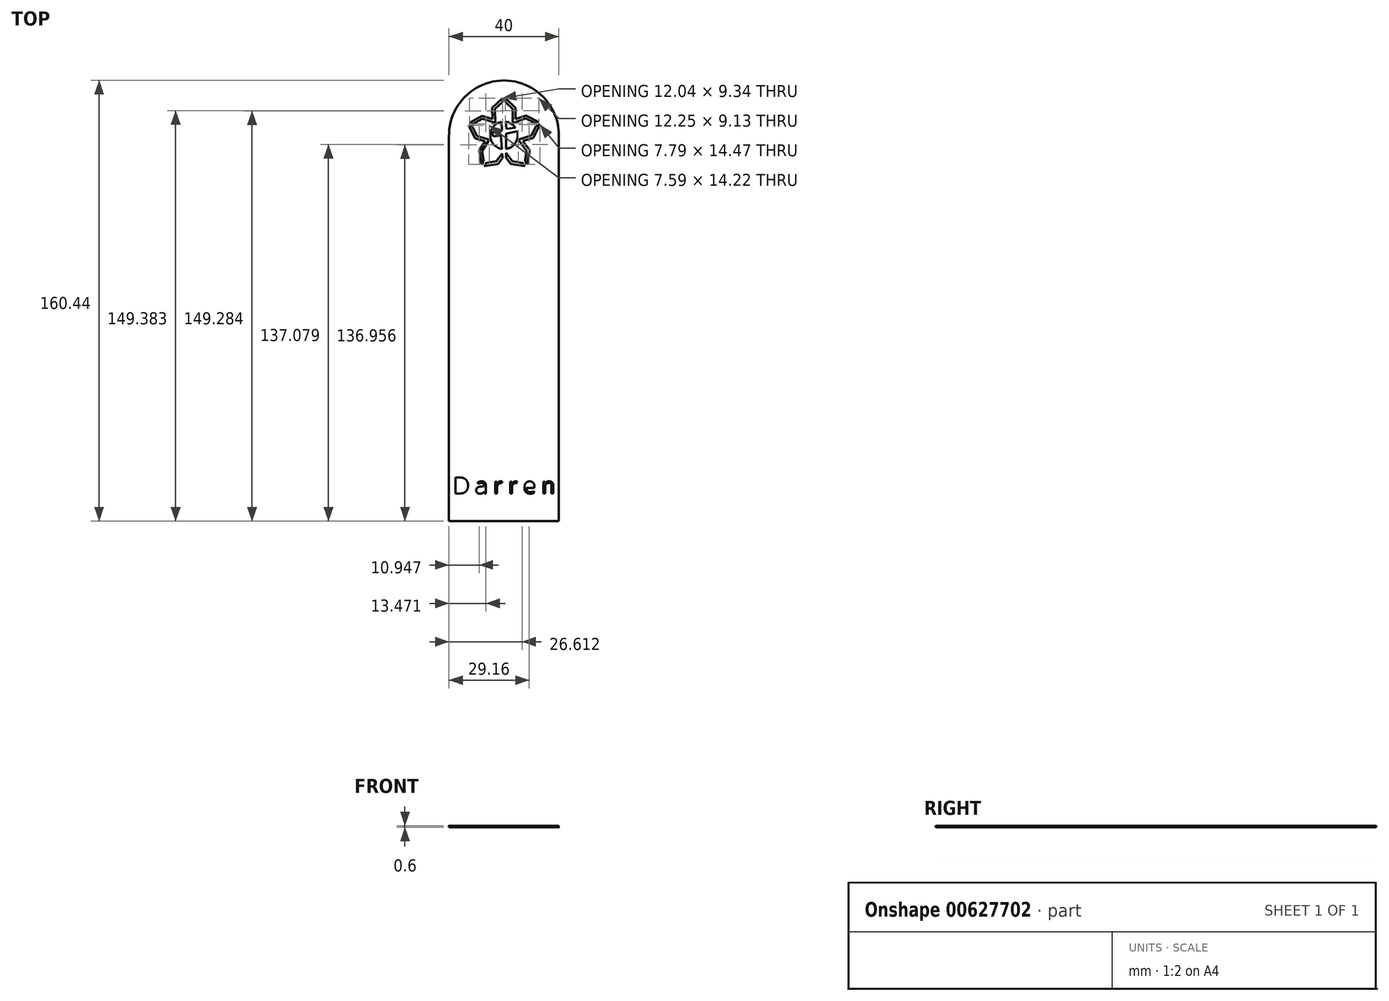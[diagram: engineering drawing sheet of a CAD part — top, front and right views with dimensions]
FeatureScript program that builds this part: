
annotation { "Feature Type Name" : "Feature", "Feature Type Description" : "" }
export const myFeature = defineFeature(function(context is Context, id is Id, definition is map)
    precondition{}
    {
        {
            var Q0;
            Q0=qCreatedBy(makeId("Top.planeOp"),FACE);
            var sketch = newSketch(context, id + "F0", { "sketchPlane" : qUnion([Q0])});
            skLineSegment(sketch, "E0", {"start": v(-29.48, 59.06) * mm, "end": v(-34.17, 60.58) * mm});
            skLineSegment(sketch, "E1", {"start": v(-34.17, 60.58) * mm, "end": v(-37.52, 58.7) * mm});
            skLineSegment(sketch, "E2", {"start": v(-37.82, 57.75) * mm, "end": v(-36.1, 54.29) * mm});
            skLineSegment(sketch, "E3", {"start": v(-36.1, 54.29) * mm, "end": v(-31.55, 52.93) * mm});
            skLineSegment(sketch, "E4", {"start": v(-31.55, 52.93) * mm, "end": v(-34.28, 48.84) * mm});
            skLineSegment(sketch, "E5", {"start": v(-34.28, 48.84) * mm, "end": v(-33.58, 45.07) * mm});
            skLineSegment(sketch, "E6", {"start": v(-32.76, 44.49) * mm, "end": v(-29.04, 45.05) * mm});
            skLineSegment(sketch, "E7", {"start": v(-29.04, 45.05) * mm, "end": v(-26.95, 47.96) * mm});
            skLineSegment(sketch, "E8", {"start": v(-25.5, 48.12) * mm, "end": v(-23.23, 45.05) * mm});
            skLineSegment(sketch, "E9", {"start": v(-23.23, 45.05) * mm, "end": v(-19.49, 44.49) * mm});
            skLineSegment(sketch, "E10", {"start": v(-18.67, 45.07) * mm, "end": v(-17.96, 48.84) * mm});
            skLineSegment(sketch, "E11", {"start": v(-17.96, 48.84) * mm, "end": v(-21.03, 52.93) * mm});
            skLineSegment(sketch, "E12", {"start": v(-21.03, 52.93) * mm, "end": v(-16.27, 54.48) * mm});
            skLineSegment(sketch, "E13", {"start": v(-16.27, 54.48) * mm, "end": v(-14.56, 57.96) * mm});
            skLineSegment(sketch, "E14", {"start": v(-14.88, 58.9) * mm, "end": v(-18.36, 60.69) * mm});
            skLineSegment(sketch, "E15", {"start": v(-18.36, 60.69) * mm, "end": v(-23.1, 59.01) * mm});
            skLineSegment(sketch, "E16", {"start": v(-23.1, 59.01) * mm, "end": v(-23.1, 64.1) * mm});
            skLineSegment(sketch, "E17", {"start": v(-23.1, 64.1) * mm, "end": v(-25.8, 66.67) * mm});
            skLineSegment(sketch, "E18", {"start": v(-26.8, 66.67) * mm, "end": v(-29.59, 64.1) * mm});
            skLineSegment(sketch, "E19", {"start": v(-29.59, 64.1) * mm, "end": v(-29.48, 59.06) * mm});
            skLineSegment(sketch, "E20", {"start": v(-25.39, 56.97) * mm, "end": v(-22.09, 57.24) * mm});
            skLineSegment(sketch, "E21", {"start": v(-25.5, 55.17) * mm, "end": v(-25.5, 49.6) * mm});
            skLineSegment(sketch, "E22", {"start": v(-26.85, 46.39) * mm, "end": v(-26.95, 47.96) * mm});
            skLineSegment(sketch, "E23", {"start": v(-27.36, 54.62) * mm, "end": v(-30.05, 54.08) * mm});
            skLineSegment(sketch, "E24", {"start": v(-30.05, 54.08) * mm, "end": v(-30.74, 55.5) * mm});
            skLineSegment(sketch, "E25", {"start": v(-30.74, 55.5) * mm, "end": v(-27.06, 56.25) * mm});
            skLineSegment(sketch, "E26", {"start": v(-27.06, 56.25) * mm, "end": v(-27.13, 59.46) * mm});
            skArc(sketch, "E27", {"start": v(-6.3, 54.09) * mm, "mid": v(-26.29, 74.53) * mm, "end": v(-46.28, 54.09) * mm});
            skLineSegment(sketch, "E28", {"start": v(-46.28, 54.09) * mm, "end": v(-46.28, -85.91) * mm});
            skLineSegment(sketch, "E29", {"start": v(-6.3, 54.09) * mm, "end": v(-6.3, -85.91) * mm});
            skLineSegment(sketch, "E30", {"start": v(-46.28, -85.91) * mm, "end": v(-6.3, -85.91) * mm});
            skLineSegment(sketch, "E31", {"start": v(-35.33, 49.06) * mm, "end": v(-33.13, 52.36) * mm});
            skLineSegment(sketch, "E32", {"start": v(-35.33, 49.06) * mm, "end": v(-34.39, 43.93) * mm});
            skLineSegment(sketch, "E33", {"start": v(-33.57, 43.35) * mm, "end": v(-28.47, 44.13) * mm});
            skLineSegment(sketch, "E34", {"start": v(-28.47, 44.13) * mm, "end": v(-26.85, 46.39) * mm});
            skLineSegment(sketch, "E35", {"start": v(-25.5, 46.44) * mm, "end": v(-23.79, 44.13) * mm});
            skLineSegment(sketch, "E36", {"start": v(-23.79, 44.13) * mm, "end": v(-18.68, 43.36) * mm});
            skLineSegment(sketch, "E37", {"start": v(-16.9, 49.09) * mm, "end": v(-17.87, 43.93) * mm});
            skLineSegment(sketch, "E38", {"start": v(-19.39, 52.41) * mm, "end": v(-16.9, 49.09) * mm});
            skLineSegment(sketch, "E39", {"start": v(-19.39, 52.41) * mm, "end": v(-15.56, 53.66) * mm});
            skLineSegment(sketch, "E40", {"start": v(-13.23, 58.4) * mm, "end": v(-15.56, 53.66) * mm});
            skLineSegment(sketch, "E41", {"start": v(-18.3, 61.77) * mm, "end": v(-13.55, 59.35) * mm});
            skLineSegment(sketch, "E42", {"start": v(-22.1, 60.43) * mm, "end": v(-18.3, 61.77) * mm});
            skLineSegment(sketch, "E43", {"start": v(-30.6, 64.53) * mm, "end": v(-26.8, 68.04) * mm});
            skLineSegment(sketch, "E44", {"start": v(-30.6, 64.53) * mm, "end": v(-30.5, 60.44) * mm});
            skLineSegment(sketch, "E45", {"start": v(-25.8, 68.04) * mm, "end": v(-22.1, 64.53) * mm});
            skLineSegment(sketch, "E46", {"start": v(-34.28, 61.66) * mm, "end": v(-30.5, 60.44) * mm});
            skLineSegment(sketch, "E47", {"start": v(-38.84, 59.11) * mm, "end": v(-34.28, 61.66) * mm});
            skLineSegment(sketch, "E48", {"start": v(-39.14, 58.16) * mm, "end": v(-36.8, 53.45) * mm});
            skLineSegment(sketch, "E49", {"start": v(-36.8, 53.45) * mm, "end": v(-33.13, 52.36) * mm});
            skLineSegment(sketch, "E50", {"start": v(-38.84, 59.11) * mm, "end": v(-37.52, 58.7) * mm});
            skLineSegment(sketch, "E51", {"start": v(-39.14, 58.16) * mm, "end": v(-37.82, 57.75) * mm});
            skLineSegment(sketch, "E52", {"start": v(-33.57, 43.35) * mm, "end": v(-32.76, 44.49) * mm});
            skLineSegment(sketch, "E53", {"start": v(-34.39, 43.93) * mm, "end": v(-33.58, 45.07) * mm});
            skLineSegment(sketch, "E54", {"start": v(-18.68, 43.36) * mm, "end": v(-19.49, 44.49) * mm});
            skLineSegment(sketch, "E55", {"start": v(-18.67, 45.07) * mm, "end": v(-17.87, 43.93) * mm});
            skLineSegment(sketch, "E56", {"start": v(-25.8, 68.04) * mm, "end": v(-25.8, 66.67) * mm});
            skLineSegment(sketch, "E57", {"start": v(-26.8, 68.04) * mm, "end": v(-26.8, 66.67) * mm});
            skLineSegment(sketch, "E58", {"start": v(-14.88, 58.9) * mm, "end": v(-13.55, 59.35) * mm});
            skLineSegment(sketch, "E59", {"start": v(-14.56, 57.96) * mm, "end": v(-13.23, 58.4) * mm});
            skLineSegment(sketch, "E60.trimOffspring", {"start": v(-22.1, 60.43) * mm, "end": v(-22.1, 64.53) * mm});
            skArc(sketch, "E61", {"start": v(-25.5, 49.6) * mm, "mid": v(-22.05, 51.88) * mm, "end": v(-21.5, 55.98) * mm});
            skLineSegment(sketch, "E62.trimOffspring", {"start": v(-27.05, 49.59) * mm, "end": v(-27.36, 54.62) * mm});
            skLineSegment(sketch, "E63.trimOffspring", {"start": v(-25.5, 48.12) * mm, "end": v(-25.5, 46.44) * mm});
            skArc(sketch, "E64.trimOffspring", {"start": v(-22.09, 57.24) * mm, "mid": v(-23.6, 58.75) * mm, "end": v(-25.6, 59.48) * mm});
            skLineSegment(sketch, "E65.trimOffspring", {"start": v(-21.5, 55.98) * mm, "end": v(-25.5, 55.17) * mm});
            skArc(sketch, "E66.trimOffspring", {"start": v(-27.13, 59.46) * mm, "mid": v(-31.29, 54.49) * mm, "end": v(-27.05, 49.59) * mm});
            skLineSegment(sketch, "E67.trimOffspring", {"start": v(-25.6, 59.48) * mm, "end": v(-25.39, 56.97) * mm});
            skSolve(sketch);
        }
        {
            var Q0;
            Q0=makeQuery(id+"F0.imprint","IMPRINT",FACE,{"disambiguationData":[TD([[makeQuery(id+"F0.imprint","IMPRINT",EDGE,{"derivedFrom":sQuery(id+"F0.wireOp",EDGE,"E0")}),1.0]])]});
            extrude(context, id + "F1", {"entities" : qUnion([Q0]), "depth" : .6 * mm, "offsetDistance" : 25 * mm});
        }
        {
            var Q0;
            Q0=makeQuery(id+"F1.opExtrude","CAP_FACE",FACE,{"disambiguationData":[OSD([sQuery(id+"F0.wireOp",EDGE,"E0"),sQuery(id+"F0.wireOp",EDGE,"E1"),sQuery(id+"F0.wireOp",EDGE,"E2"),sQuery(id+"F0.wireOp",EDGE,"E3"),sQuery(id+"F0.wireOp",EDGE,"E4"),sQuery(id+"F0.wireOp",EDGE,"E5"),sQuery(id+"F0.wireOp",EDGE,"E6"),sQuery(id+"F0.wireOp",EDGE,"E7"),sQuery(id+"F0.wireOp",EDGE,"E8"),sQuery(id+"F0.wireOp",EDGE,"E9"),sQuery(id+"F0.wireOp",EDGE,"E10"),sQuery(id+"F0.wireOp",EDGE,"E11"),sQuery(id+"F0.wireOp",EDGE,"E12"),sQuery(id+"F0.wireOp",EDGE,"E13"),sQuery(id+"F0.wireOp",EDGE,"E14"),sQuery(id+"F0.wireOp",EDGE,"E15"),sQuery(id+"F0.wireOp",EDGE,"E16"),sQuery(id+"F0.wireOp",EDGE,"E17"),sQuery(id+"F0.wireOp",EDGE,"E18"),sQuery(id+"F0.wireOp",EDGE,"E19"),sQuery(id+"F0.wireOp",EDGE,"E20"),sQuery(id+"F0.wireOp",EDGE,"E21"),sQuery(id+"F0.wireOp",EDGE,"E22"),sQuery(id+"F0.wireOp",EDGE,"E23"),sQuery(id+"F0.wireOp",EDGE,"E24"),sQuery(id+"F0.wireOp",EDGE,"E25"),sQuery(id+"F0.wireOp",EDGE,"E26"),sQuery(id+"F0.wireOp",EDGE,"E27"),sQuery(id+"F0.wireOp",EDGE,"E28"),sQuery(id+"F0.wireOp",EDGE,"E29"),sQuery(id+"F0.wireOp",EDGE,"E30"),sQuery(id+"F0.wireOp",EDGE,"E31"),sQuery(id+"F0.wireOp",EDGE,"E32"),sQuery(id+"F0.wireOp",EDGE,"E33"),sQuery(id+"F0.wireOp",EDGE,"E34"),sQuery(id+"F0.wireOp",EDGE,"E35"),sQuery(id+"F0.wireOp",EDGE,"E36"),sQuery(id+"F0.wireOp",EDGE,"E37"),sQuery(id+"F0.wireOp",EDGE,"E38"),sQuery(id+"F0.wireOp",EDGE,"E39"),sQuery(id+"F0.wireOp",EDGE,"E40"),sQuery(id+"F0.wireOp",EDGE,"E41"),sQuery(id+"F0.wireOp",EDGE,"E42"),sQuery(id+"F0.wireOp",EDGE,"E43"),sQuery(id+"F0.wireOp",EDGE,"E44"),sQuery(id+"F0.wireOp",EDGE,"E45"),sQuery(id+"F0.wireOp",EDGE,"E46"),sQuery(id+"F0.wireOp",EDGE,"E47"),sQuery(id+"F0.wireOp",EDGE,"E48"),sQuery(id+"F0.wireOp",EDGE,"E49"),sQuery(id+"F0.wireOp",EDGE,"E50"),sQuery(id+"F0.wireOp",EDGE,"E51"),sQuery(id+"F0.wireOp",EDGE,"E52"),sQuery(id+"F0.wireOp",EDGE,"E53"),sQuery(id+"F0.wireOp",EDGE,"E54"),sQuery(id+"F0.wireOp",EDGE,"E55"),sQuery(id+"F0.wireOp",EDGE,"E56"),sQuery(id+"F0.wireOp",EDGE,"E57"),sQuery(id+"F0.wireOp",EDGE,"E58"),sQuery(id+"F0.wireOp",EDGE,"E59"),sQuery(id+"F0.wireOp",EDGE,"E60.trimOffspring"),sQuery(id+"F0.wireOp",EDGE,"E61"),sQuery(id+"F0.wireOp",EDGE,"E62.trimOffspring"),sQuery(id+"F0.wireOp",EDGE,"E63.trimOffspring"),sQuery(id+"F0.wireOp",EDGE,"E64.trimOffspring"),sQuery(id+"F0.wireOp",EDGE,"E65.trimOffspring"),sQuery(id+"F0.wireOp",EDGE,"E66.trimOffspring"),sQuery(id+"F0.wireOp",EDGE,"E67.trimOffspring")])],"isStart":false});
            var sketch = newSketch(context, id + "F2", { "sketchPlane" : qUnion([Q0])});
            skText(sketch, "E68", { "text": "D a r r e n", "fontName": "OpenSans-Regular.ttf"});
            const initialGuessF2  = {"E68": [-0.04478, -0.07591, 1, 0, 0.00584]};
            skSetInitialGuess(sketch, initialGuessF2);
            skSolve(sketch);
        }
        {
            var Q0;
            Q0=makeQuery(id+"F2.imprint","IMPRINT",FACE,{"disambiguationData":[TD([[makeQuery(id+"F2.imprint","IMPRINT",EDGE,{"derivedFrom":sQuery(id+"F2.wireOp",EDGE,"E68.sketch_text.stroke-7")}),1.0]])]});
            var Q1;
            Q1=makeQuery(id+"F2.imprint","IMPRINT",FACE,{"disambiguationData":[TD([[makeQuery(id+"F2.imprint","IMPRINT",EDGE,{"derivedFrom":sQuery(id+"F2.wireOp",EDGE,"E68.sketch_text.stroke-0")}),-1.0]])]});
            var Q2;
            Q2=makeQuery(id+"F2.imprint","IMPRINT",FACE,{"disambiguationData":[TD([[makeQuery(id+"F2.imprint","IMPRINT",EDGE,{"derivedFrom":sQuery(id+"F2.wireOp",EDGE,"E68.sketch_text.stroke-33")}),1.0]])]});
            var Q3;
            Q3=makeQuery(id+"F2.imprint","IMPRINT",FACE,{"disambiguationData":[TD([[makeQuery(id+"F2.imprint","IMPRINT",EDGE,{"derivedFrom":sQuery(id+"F2.wireOp",EDGE,"E68.sketch_text.stroke-14")}),-1.0]])]});
            var Q4;
            Q4=makeQuery(id+"F2.imprint","IMPRINT",FACE,{"disambiguationData":[TD([[makeQuery(id+"F2.imprint","IMPRINT",EDGE,{"derivedFrom":sQuery(id+"F2.wireOp",EDGE,"E68.sketch_text.stroke-41")}),-1.0]])]});
            var Q5;
            Q5=makeQuery(id+"F2.imprint","IMPRINT",FACE,{"disambiguationData":[TD([[makeQuery(id+"F2.imprint","IMPRINT",EDGE,{"derivedFrom":sQuery(id+"F2.wireOp",EDGE,"E68.sketch_text.stroke-54")}),-1.0]])]});
            var Q6;
            Q6=makeQuery(id+"F2.imprint","IMPRINT",FACE,{"disambiguationData":[TD([[makeQuery(id+"F2.imprint","IMPRINT",EDGE,{"derivedFrom":sQuery(id+"F2.wireOp",EDGE,"E68.sketch_text.stroke-81")}),1.0]])]});
            var Q7;
            Q7=makeQuery(id+"F2.imprint","IMPRINT",FACE,{"disambiguationData":[TD([[makeQuery(id+"F2.imprint","IMPRINT",EDGE,{"derivedFrom":sQuery(id+"F2.wireOp",EDGE,"E68.sketch_text.stroke-67")}),-1.0]])]});
            var Q8;
            Q8=makeQuery(id+"F2.imprint","IMPRINT",FACE,{"disambiguationData":[TD([[makeQuery(id+"F2.imprint","IMPRINT",EDGE,{"derivedFrom":sQuery(id+"F2.wireOp",EDGE,"E68.sketch_text.stroke-86")}),-1.0]])]});
            extrude(context, id + "F3", {"entities" : qUnion([Q0, Q1, Q2, Q3, Q4, Q5, Q6, Q7, Q8]), "operationType" : NewBodyOperationType.REMOVE, "oppositeDirection" : true, "depth" : 25 * mm, "offsetDistance" : 25 * mm});
        }
    });
